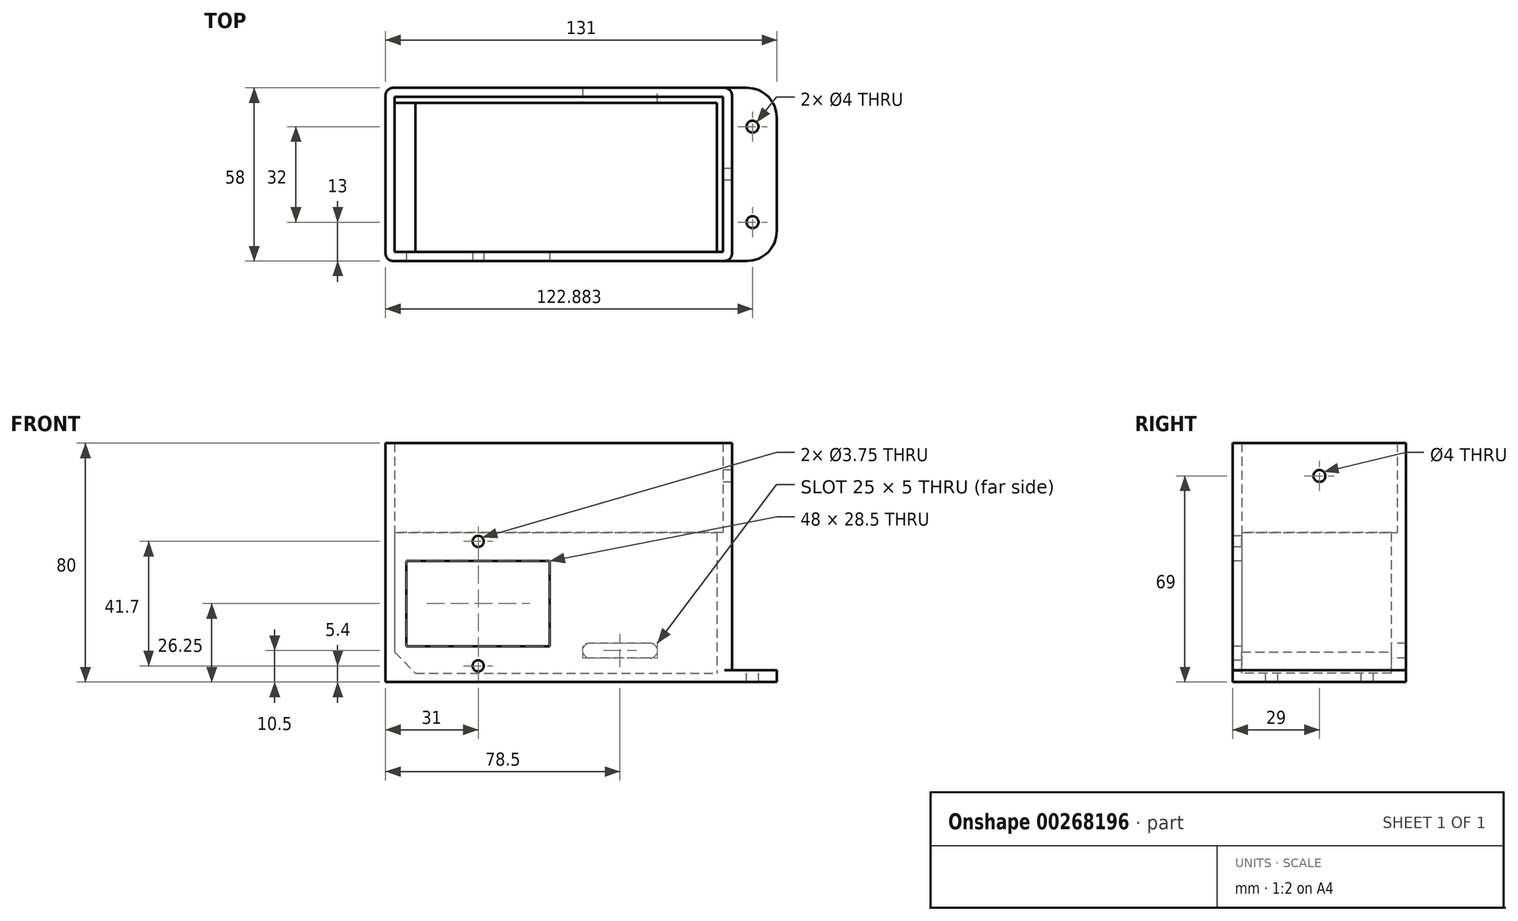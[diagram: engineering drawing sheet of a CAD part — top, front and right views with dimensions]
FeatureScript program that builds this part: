
annotation { "Feature Type Name" : "Feature", "Feature Type Description" : "" }
export const myFeature = defineFeature(function(context is Context, id is Id, definition is map)
    precondition{}
    {
        {
            var Q0;
            Q0=qCreatedBy(makeId("Top.planeOp"),FACE);
            var sketch = newSketch(context, id + "F0", { "sketchPlane" : qUnion([Q0])});
            skLineSegment(sketch, "E0.bottom", {"start": v(58, -29) * mm, "end": v(-58, -29) * mm});
            skLineSegment(sketch, "E0.top", {"start": v(58, 29) * mm, "end": v(-58, 29) * mm});
            skLineSegment(sketch, "E0.left", {"start": v(58, -29) * mm, "end": v(58, 29) * mm});
            skLineSegment(sketch, "E0.right", {"start": v(-58, -29) * mm, "end": v(-58, 29) * mm});
            skPoint(sketch, "E0.middle", {"position": v(0, 0) * mm});
            skSolve(sketch);
        }
        {
            var Q0;
            Q0 = qSketchRegion(id + "F0", true);
            extrude(context, id + "F1", {"entities" : qUnion([Q0]), "depth" : 80 * mm});
        }
        {
            var Q0;
            Q0=makeQuery(id+"F1.opExtrude","CAP_FACE",FACE,{"disambiguationData":[OSD([sQuery(id+"F0.wireOp",EDGE,"E0.bottom"),sQuery(id+"F0.wireOp",EDGE,"E0.top"),sQuery(id+"F0.wireOp",EDGE,"E0.left"),sQuery(id+"F0.wireOp",EDGE,"E0.right")])],"isStart":false});
            shell(context, id + "F2", {"entities" : qUnion([Q0]), "thickness" : 3 * mm});
        }
        {
            var Q0;
            Q0=makeQuery(id+"F2.opShell","OFFSET_FACE",FACE,{"disambiguationData":[OSD([sQuery(id+"F0.wireOp",EDGE,"E0.bottom"),sQuery(id+"F0.wireOp",EDGE,"E0.top"),sQuery(id+"F0.wireOp",EDGE,"E0.left"),sQuery(id+"F0.wireOp",EDGE,"E0.right")])]});
            var sketch = newSketch(context, id + "F3", { "sketchPlane" : qUnion([Q0])});
            skLineSegment(sketch, "E1", {"start": v(-55, 24) * mm, "end": v(53, 24) * mm});
            skLineSegment(sketch, "E2", {"start": v(53, 24) * mm, "end": v(53, -26) * mm});
            skSolve(sketch);
        }
        {
            var Q0;
            Q0 = qSketchRegion(id + "F3", true);
            var Q1;
            {var subQ5=sQuery(id+"F3.wireOp",EDGE,"E1");Q1=makeQuery(id+"F3.imprint","IMPRINT",FACE,{"disambiguationData":[TD([[makeQuery(id+"F3.imprint","IMPRINT",EDGE,{"derivedFrom":subQ5}),1.0]])]});}
            extrude(context, id + "F4", {"entities" : qUnion([Q0, Q1]), "operationType" : NewBodyOperationType.ADD, "depth" : 47 * mm});
        }
        {
            var Q0;
            Q0=makeQuery(id+"F2.opShell","OFFSET_FACE",FACE,{"disambiguationData":[OSD([sQuery(id+"F0.wireOp",EDGE,"E0.left")])]});
            var sketch = newSketch(context, id + "F5", { "sketchPlane" : qUnion([Q0])});
            skCircle(sketch, "E3", {"center": v(0, 69) * mm, "radius": 2 * mm});
            skPoint(sketch, "E3.centerSnap0", {"position": v(0, 50) * mm});
            skSolve(sketch);
        }
        {
            var Q0;
            Q0 = qSketchRegion(id + "F5", true);
            extrude(context, id + "F6", {"entities" : qUnion([Q0]), "operationType" : NewBodyOperationType.REMOVE, "endBound" : BoundingType.THROUGH_ALL, "oppositeDirection" : true, "depth" : 25 * mm});
        }
        {
            var Q0;
            Q0=makeQuery(id+"F1.opExtrude","SWEPT_FACE",FACE,{"disambiguationData":[OSD([sQuery(id+"F0.wireOp",EDGE,"E0.left")])]});
            var sketch = newSketch(context, id + "F7", { "sketchPlane" : qUnion([Q0])});
            skLineSegment(sketch, "E4.bottom", {"start": v(29, 0) * mm, "end": v(-29, 0) * mm});
            skLineSegment(sketch, "E4.top", {"start": v(29, 4) * mm, "end": v(-29, 4) * mm});
            skLineSegment(sketch, "E4.left", {"start": v(29, 0) * mm, "end": v(29, 4) * mm});
            skLineSegment(sketch, "E4.right", {"start": v(-29, 0) * mm, "end": v(-29, 4) * mm});
            skSolve(sketch);
        }
        {
            var Q0;
            Q0 = qSketchRegion(id + "F7", true);
            extrude(context, id + "F8", {"entities" : qUnion([Q0]), "operationType" : NewBodyOperationType.ADD, "depth" : 15 * mm});
        }
        {
            var Q0;
            Q0=makeQuery(id+"F8.opExtrude","CAP_EDGE",EDGE,{"disambiguationData":[OSD([sQuery(id+"F7.wireOp",EDGE,"E4.left")])],"isStart":false});
            var Q1;
            Q1=makeQuery(id+"F8.opExtrude","CAP_EDGE",EDGE,{"disambiguationData":[OSD([sQuery(id+"F7.wireOp",EDGE,"E4.right")])],"isStart":false});
            fillet(context, id + "F9", {"entities" : qUnion([Q0, Q1]), "radius" : 10 * mm, "tangentPropagation" : true, "allowEdgeOverflow" : false});
        }
        {
            var Q0;
            Q0=makeQuery(id+"F8.opExtrude","SWEPT_FACE",FACE,{"disambiguationData":[OSD([sQuery(id+"F7.wireOp",EDGE,"E4.top")])]});
            var sketch = newSketch(context, id + "F10", { "sketchPlane" : qUnion([Q0])});
            skCircle(sketch, "E5", {"center": v(64.88, 16) * mm, "radius": 2 * mm});
            skCircle(sketch, "E6", {"center": v(64.88, -16) * mm, "radius": 2 * mm});
            skSolve(sketch);
        }
        {
            var Q0;
            Q0 = qSketchRegion(id + "F10", true);
            extrude(context, id + "F11", {"entities" : qUnion([Q0]), "operationType" : NewBodyOperationType.REMOVE, "endBound" : BoundingType.THROUGH_ALL, "oppositeDirection" : true, "depth" : 25 * mm});
        }
        {
            var Q0;
            {var subQ0=sQuery(id+"F7.wireOp",EDGE,"E4.right");Q0=makeQuery(id+"F8GR8ETMVvvvEQZ_1.1.F8.boolean.opBoolean","MERGE",FACE,{"derivedFrom":[makeQuery(id+"F8.boolean.opBoolean","MERGE",FACE,{"derivedFrom":[makeQuery(id+"F1.opExtrude","SWEPT_FACE",FACE,{"disambiguationData":[OSD([sQuery(id+"F0.wireOp",EDGE,"E0.bottom")])]}),makeQuery(id+"F8.opExtrude","SWEPT_FACE",FACE,{"disambiguationData":[OSD([subQ0])]})]}),makeQuery(id+"F8GR8ETMVvvvEQZ_1.1.F8.opExtrude","SWEPT_FACE",FACE,{"disambiguationData":[OSD([subQ0])]})]});}
            var sketch = newSketch(context, id + "F12", { "sketchPlane" : qUnion([Q0])});
            skLineSegment(sketch, "E7.bottom", {"start": v(-51, 40.5) * mm, "end": v(-3, 40.5) * mm});
            skLineSegment(sketch, "E7.top", {"start": v(-51, 12) * mm, "end": v(-3, 12) * mm});
            skLineSegment(sketch, "E7.left", {"start": v(-51, 40.5) * mm, "end": v(-51, 12) * mm});
            skLineSegment(sketch, "E7.right", {"start": v(-3, 40.5) * mm, "end": v(-3, 12) * mm});
            skSolve(sketch);
        }
        {
            var Q0;
            Q0 = qSketchRegion(id + "F12", true);
            extrude(context, id + "F13", {"entities" : qUnion([Q0]), "operationType" : NewBodyOperationType.REMOVE, "oppositeDirection" : true, "depth" : 5 * mm});
        }
        {
            var Q0;
            {var subQ0=sQuery(id+"F7.wireOp",EDGE,"E4.right");Q0=makeQuery(id+"F8GR8ETMVvvvEQZ_1.1.F8.boolean.opBoolean","MERGE",FACE,{"derivedFrom":[makeQuery(id+"F8.boolean.opBoolean","MERGE",FACE,{"derivedFrom":[makeQuery(id+"F1.opExtrude","SWEPT_FACE",FACE,{"disambiguationData":[OSD([sQuery(id+"F0.wireOp",EDGE,"E0.bottom")])]}),makeQuery(id+"F8.opExtrude","SWEPT_FACE",FACE,{"disambiguationData":[OSD([subQ0])]})]}),makeQuery(id+"F8GR8ETMVvvvEQZ_1.1.F8.opExtrude","SWEPT_FACE",FACE,{"disambiguationData":[OSD([subQ0])]})]});}
            var sketch = newSketch(context, id + "F14", { "sketchPlane" : qUnion([Q0])});
            skCircle(sketch, "E8", {"center": v(-27, 47.1) * mm, "radius": 1.88 * mm});
            skPoint(sketch, "E8.centerSnap0", {"position": v(-27, 40.5) * mm});
            skCircle(sketch, "E9", {"center": v(-27, 5.4) * mm, "radius": 1.88 * mm});
            skPoint(sketch, "E9.centerSnap0", {"position": v(-27, 12) * mm});
            skSolve(sketch);
        }
        {
            var Q0;
            Q0 = qSketchRegion(id + "F14", true);
            extrude(context, id + "F15", {"entities" : qUnion([Q0]), "operationType" : NewBodyOperationType.REMOVE, "oppositeDirection" : true, "depth" : 5 * mm});
        }
        {
            var Q0;
            Q0=makeQuery(id+"F4.opExtrude","SWEPT_FACE",FACE,{"disambiguationData":[OSD([sQuery(id+"F3.wireOp",EDGE,"E1")])]});
            var sketch = newSketch(context, id + "F16", { "sketchPlane" : qUnion([Q0])});
            skLineSegment(sketch, "E10.bottom", {"start": v(33, 8) * mm, "end": v(8, 8) * mm});
            skLineSegment(sketch, "E10.top", {"start": v(33, 13) * mm, "end": v(8, 13) * mm});
            skLineSegment(sketch, "E10.left", {"start": v(33, 8) * mm, "end": v(33, 13) * mm});
            skLineSegment(sketch, "E10.right", {"start": v(8, 8) * mm, "end": v(8, 13) * mm});
            skSolve(sketch);
        }
        {
            var Q0;
            Q0 = qSketchRegion(id + "F16", true);
            extrude(context, id + "F17", {"entities" : qUnion([Q0]), "operationType" : NewBodyOperationType.REMOVE, "endBound" : BoundingType.THROUGH_ALL, "oppositeDirection" : true, "depth" : 25 * mm});
        }
        {
            var Q0;
            Q0=makeQuery(id+"F17.boolean.opBoolean","COPY",EDGE,{"derivedFrom":makeQuery(id+"F17.opExtrude","SWEPT_EDGE",EDGE,{"disambiguationData":[OSD([sQuery(id+"F16.wireOp",EDGE,"E10.top"),sQuery(id+"F16.wireOp",EDGE,"E10.left")])]})});
            var Q1;
            Q1=makeQuery(id+"F17.boolean.opBoolean","COPY",EDGE,{"derivedFrom":makeQuery(id+"F17.opExtrude","SWEPT_EDGE",EDGE,{"disambiguationData":[OSD([sQuery(id+"F16.wireOp",EDGE,"E10.top"),sQuery(id+"F16.wireOp",EDGE,"E10.right")])]})});
            var Q2;
            Q2=makeQuery(id+"F17.boolean.opBoolean","COPY",EDGE,{"derivedFrom":makeQuery(id+"F17.opExtrude","SWEPT_EDGE",EDGE,{"disambiguationData":[OSD([sQuery(id+"F16.wireOp",EDGE,"E10.bottom"),sQuery(id+"F16.wireOp",EDGE,"E10.left")])]})});
            var Q3;
            Q3=makeQuery(id+"F17.boolean.opBoolean","COPY",EDGE,{"derivedFrom":makeQuery(id+"F17.opExtrude","SWEPT_EDGE",EDGE,{"disambiguationData":[OSD([sQuery(id+"F16.wireOp",EDGE,"E10.bottom"),sQuery(id+"F16.wireOp",EDGE,"E10.right")])]})});
            fillet(context, id + "F18", {"entities" : qUnion([Q0, Q1, Q2, Q3]), "radius" : 2.5 * mm, "tangentPropagation" : true, "allowEdgeOverflow" : false});
        }
        {
            var Q0;
            Q0=makeQuery(id+"F1.opExtrude","SWEPT_EDGE",EDGE,{"disambiguationData":[OSD([sQuery(id+"F0.wireOp",EDGE,"E0.bottom"),sQuery(id+"F0.wireOp",EDGE,"E0.right")])]});
            var Q1;
            Q1=makeQuery(id+"F1.opExtrude","SWEPT_EDGE",EDGE,{"disambiguationData":[OSD([sQuery(id+"F0.wireOp",EDGE,"E0.bottom"),sQuery(id+"F0.wireOp",EDGE,"E0.left")])]});
            var Q2;
            Q2=makeQuery(id+"F1.opExtrude","SWEPT_EDGE",EDGE,{"disambiguationData":[OSD([sQuery(id+"F0.wireOp",EDGE,"E0.top"),sQuery(id+"F0.wireOp",EDGE,"E0.left")])]});
            var Q3;
            Q3=makeQuery(id+"F1.opExtrude","SWEPT_EDGE",EDGE,{"disambiguationData":[OSD([sQuery(id+"F0.wireOp",EDGE,"E0.top"),sQuery(id+"F0.wireOp",EDGE,"E0.right")])]});
            fillet(context, id + "F19", {"entities" : qUnion([Q0, Q1, Q2, Q3]), "radius" : 2.5 * mm, "tangentPropagation" : true, "allowEdgeOverflow" : false});
        }
        {
            var Q0;
            {var subQ0=sQuery(id+"F0.wireOp",EDGE,"E0.right");Q0=makeQuery(id+"F2.opShell","OFFSET_EDGE",EDGE,{"disambiguationData":[OSD([subQ0]),TDD([makeQuery(id+"F1.opExtrude","CAP_EDGE",EDGE,{"disambiguationData":[OSD([subQ0])],"isStart":true})])]});}
            var Q1;
            Q1=makeQuery(id+"F4.opExtrude","CAP_EDGE",EDGE,{"disambiguationData":[OSD([sQuery(id+"F3.wireOp",EDGE,"E2")])],"isStart":true});
            chamfer(context, id + "F20", {"entities" : qUnion([Q0, Q1]), "width" : 7 * mm, "tangentPropagation" : true});
        }
    });
